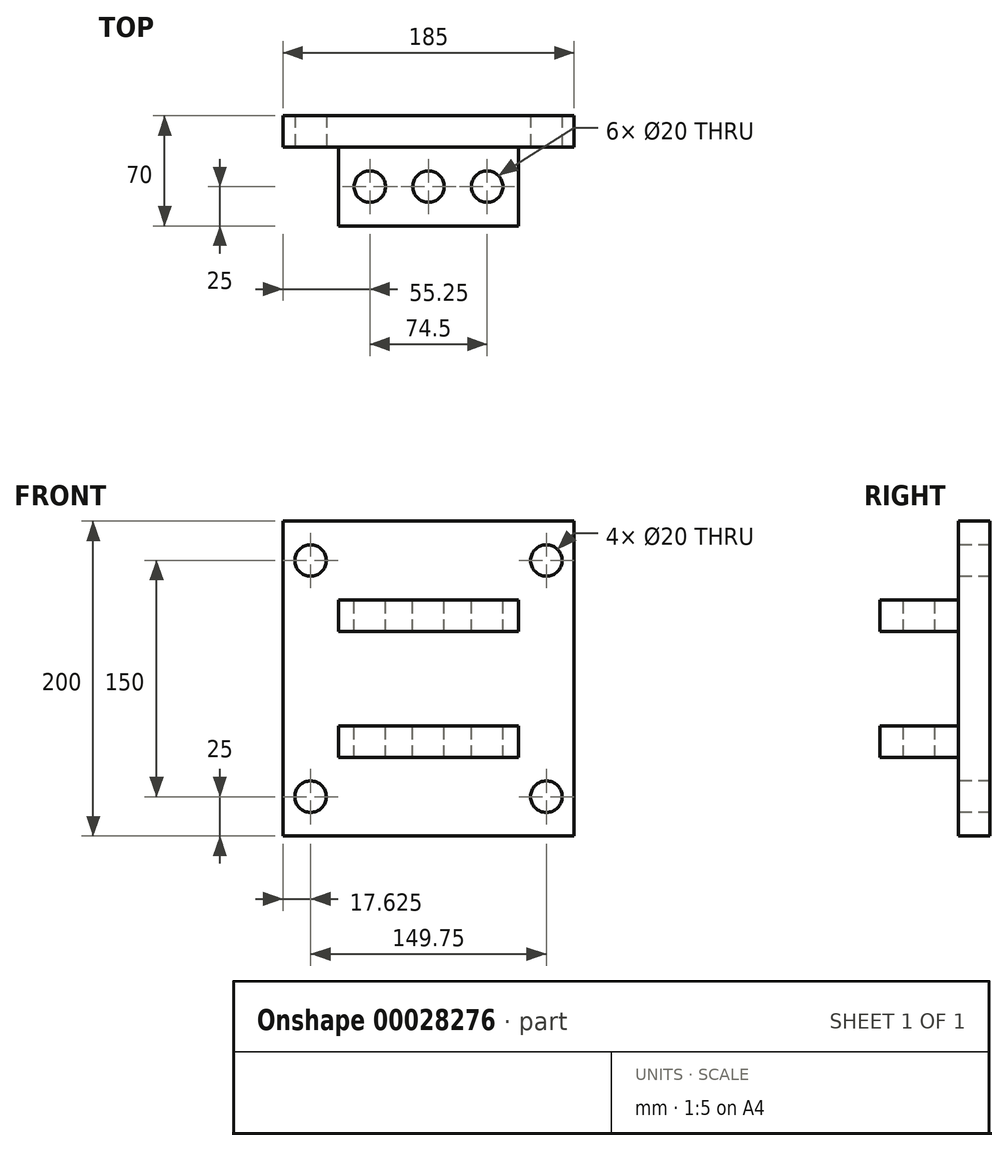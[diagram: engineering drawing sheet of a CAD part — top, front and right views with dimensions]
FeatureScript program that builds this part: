
annotation { "Feature Type Name" : "Feature", "Feature Type Description" : "" }
export const myFeature = defineFeature(function(context is Context, id is Id, definition is map)
    precondition{}
    {
        {
            var Q0;
            Q0=qCreatedBy(makeId("Front.planeOp"),FACE);
            var sketch = newSketch(context, id + "F0", { "sketchPlane" : qUnion([Q0])});
            skLineSegment(sketch, "E0.rect.bottom", {"start": v(92.5, -100) * mm, "end": v(-92.5, -100) * mm});
            skLineSegment(sketch, "E0.rect.top", {"start": v(92.5, 100) * mm, "end": v(-92.5, 100) * mm});
            skLineSegment(sketch, "E0.rect.left", {"start": v(92.5, -100) * mm, "end": v(92.5, 100) * mm});
            skLineSegment(sketch, "E0.rect.right", {"start": v(-92.5, -100) * mm, "end": v(-92.5, 100) * mm});
            skPoint(sketch, "E0.rect.middle", {"position": v(0, 0) * mm});
            skSolve(sketch);
        }
        {
            var Q0;
            Q0 = qSketchRegion(id + "F0", true);
            extrude(context, id + "F1", {"entities" : qUnion([Q0]), "depth" : 20 * mm});
        }
        {
            var Q0;
            Q0=makeQuery(id+"F1.opExtrude","CAP_FACE",FACE,{"disambiguationData":[OSD([sQuery(id+"F0.wireOp",EDGE,"E0.rect.bottom"),sQuery(id+"F0.wireOp",EDGE,"E0.rect.top"),sQuery(id+"F0.wireOp",EDGE,"E0.rect.left"),sQuery(id+"F0.wireOp",EDGE,"E0.rect.right")])],"isStart":false});
            var sketch = newSketch(context, id + "F2", { "sketchPlane" : qUnion([Q0])});
            skLineSegment(sketch, "E1", {"start": v(-92.5, 0) * mm, "end": v(92.5, 0) * mm});
            skLineSegment(sketch, "E2.0", {"start": v(-57.25, -30) * mm, "end": v(57.25, -30) * mm});
            skLineSegment(sketch, "E3.0", {"start": v(-57.25, -50) * mm, "end": v(57.25, -50) * mm});
            skLineSegment(sketch, "E4.0", {"start": v(-57.25, 30) * mm, "end": v(57.25, 30) * mm});
            skLineSegment(sketch, "E5.0", {"start": v(-57.25, 50) * mm, "end": v(57.25, 50) * mm});
            skLineSegment(sketch, "E6", {"start": v(0, 50) * mm, "end": v(57.25, 50) * mm});
            skLineSegment(sketch, "E7", {"start": v(57.25, 50) * mm, "end": v(57.25, 30) * mm});
            skLineSegment(sketch, "E8", {"start": v(57.25, -50) * mm, "end": v(-57.25, -50) * mm});
            skLineSegment(sketch, "E9.trimOffspring", {"start": v(-57.25, -30) * mm, "end": v(-57.25, -50) * mm});
            skLineSegment(sketch, "E10.trimOffspring", {"start": v(57.25, -30) * mm, "end": v(57.25, -50) * mm});
            skLineSegment(sketch, "E11", {"start": v(-57.25, 50) * mm, "end": v(-57.25, 30) * mm});
            skSolve(sketch);
        }
        {
            var Q0;
            Q0 = qSketchRegion(id + "F2", true);
            extrude(context, id + "F3", {"entities" : qUnion([Q0]), "operationType" : NewBodyOperationType.ADD, "depth" : 50 * mm});
        }
        {
            var Q0;
            Q0=makeQuery(id+"F3.opExtrude","SWEPT_FACE",FACE,{"disambiguationData":[OSD([sQuery(id+"F2.wireOp",EDGE,"E5.0")])]});
            var sketch = newSketch(context, id + "F4", { "sketchPlane" : qUnion([Q0])});
            skLineSegment(sketch, "E12", {"start": v(92.5, -70) * mm, "end": v(92.5, -45) * mm});
            skLineSegment(sketch, "E13", {"start": v(92.5, -45) * mm, "end": v(-92.5, -45) * mm});
            skCircle(sketch, "E14", {"center": v(0, -45) * mm, "radius": 10 * mm});
            skCircle(sketch, "E15", {"center": v(37.25, -45) * mm, "radius": 10 * mm});
            skCircle(sketch, "E16", {"center": v(-37.25, -45) * mm, "radius": 10 * mm});
            skSolve(sketch);
        }
        {
            var Q0;
            Q0 = qSketchRegion(id + "F4", true);
            extrude(context, id + "F5", {"entities" : qUnion([Q0]), "operationType" : NewBodyOperationType.REMOVE, "oppositeDirection" : true, "depth" : 166.32 * mm, "hasSecondDirection" : true, "secondDirectionOppositeDirection" : false, "secondDirectionDepth" : 96.54 * mm});
        }
        {
            var Q0;
            Q0=makeQuery(id+"F1.opExtrude","CAP_FACE",FACE,{"disambiguationData":[OSD([sQuery(id+"F0.wireOp",EDGE,"E0.rect.bottom"),sQuery(id+"F0.wireOp",EDGE,"E0.rect.top"),sQuery(id+"F0.wireOp",EDGE,"E0.rect.left"),sQuery(id+"F0.wireOp",EDGE,"E0.rect.right")])],"isStart":false});
            var sketch = newSketch(context, id + "F6", { "sketchPlane" : qUnion([Q0])});
            skLineSegment(sketch, "E17", {"start": v(-57.25, 50) * mm, "end": v(-92.5, 50) * mm});
            skLineSegment(sketch, "E18", {"start": v(-74.87, 50) * mm, "end": v(-74.87, 100) * mm});
            skLineSegment(sketch, "E19", {"start": v(-74.87, 50) * mm, "end": v(-74.87, -100) * mm});
            skCircle(sketch, "E20", {"center": v(-74.87, 75) * mm, "radius": 10 * mm});
            skLineSegment(sketch, "E21", {"start": v(0, 0) * mm, "end": v(0, 15.84) * mm});
            skLineSegment(sketch, "E22", {"start": v(-92.5, 0) * mm, "end": v(-69.22, 0) * mm});
            skCircle(sketch, "E23.MirrorC", {"center": v(-74.87, -75) * mm, "radius": 10 * mm});
            skCircle(sketch, "E24.MirrorC", {"center": v(74.87, 75) * mm, "radius": 10 * mm});
            skCircle(sketch, "E25.MirrorC", {"center": v(74.87, -75) * mm, "radius": 10 * mm});
            skSolve(sketch);
        }
        {
            var Q0;
            Q0 = qSketchRegion(id + "F6", true);
            extrude(context, id + "F7", {"entities" : qUnion([Q0]), "operationType" : NewBodyOperationType.REMOVE, "oppositeDirection" : true, "depth" : 25 * mm});
        }
    });
